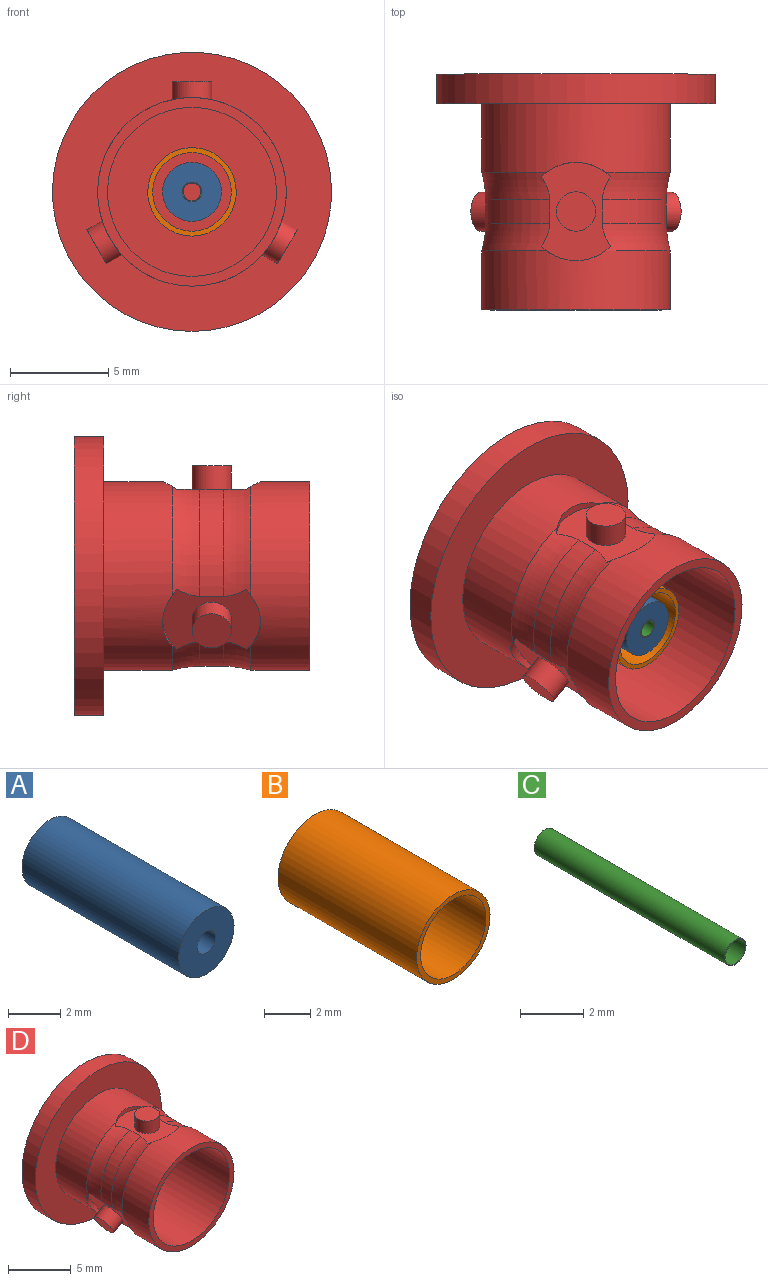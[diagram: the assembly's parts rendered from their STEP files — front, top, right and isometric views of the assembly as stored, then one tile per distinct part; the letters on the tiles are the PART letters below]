
ASSEMBLY  parts=4 mates=3
PART A: 4 faces, bbox 3x8.5x3 mm
  f0: cylinder r=0.5mm len=8.5mm, axis (0,1,0), area 26.7mm2, adj f2,f3
  f1: cylinder r=1.5mm len=8.5mm, axis (0,1,0), area 80.1mm2, adj f2,f3
  f2: plane 3x3mm, normal (0,-1,0), area 6.3mm2, adj f0,f1
  f3: plane 3x3mm, normal (0,1,0), area 6.3mm2, adj f0,f1
PART B: 4 faces, bbox 4.5x8.5x4.5 mm
  f0: cylinder r=2mm len=8.5mm, axis (0,1,0), area 106.8mm2, adj f2,f3
  f1: cylinder r=2.25mm len=8.5mm, axis (0,1,0), area 120.2mm2, adj f2,f3
  f2: plane 4.5x4.5mm, normal (0,-1,0), area 3.3mm2, adj f0,f1
  f3: plane 4.5x4.5mm, normal (0,1,0), area 3.3mm2, adj f0,f1
PART C: 4 faces, bbox 1x8.5x1 mm
  f0: cylinder r=0.45mm len=8.5mm, axis (0,1,0), area 24mm2, adj f2,f3
  f1: cylinder r=0.47mm len=8.5mm, axis (0,1,0), area 25.4mm2, adj f2,f3
  f2: plane 0.95x0.95mm, normal (0,-1,0), area 0.1mm2, adj f0,f1
  f3: plane 0.95x0.95mm, normal (0,1,0), area 0.1mm2, adj f0,f1
PART D: 32 faces, bbox 14.2x12x14.2 mm
  f0: plane 2x1.73mm, normal (0.87,0,-0.5), area 3.1mm2, adj f1
  f1: cylinder r=1mm len=2.33mm, axis (0.87,0,-0.5), area 7.5mm2, adj f0,f8
  f2: plane 2x1.73mm, normal (-0.87,0,-0.5), area 3.1mm2, adj f3
  f3: cylinder r=1mm len=2.33mm, axis (-0.87,0,-0.5), area 7.5mm2, adj f2,f6
  f4: cylinder r=4.8mm len=9.6mm, axis (0,1,0), area 102.5mm2, adj f5,f7,f9,f17,f27,f28,f30
  f5: cylinder r=2.5mm len=3.25mm, axis (-0.87,0,-0.5), area 1.1mm2, adj f4,f6,f27,f28
  f6: plane 5x3.05mm, normal (-0.87,0,-0.5), area 10.6mm2, adj f3,f5,f19,f23,f24,f25,f26,f27
  f7: cylinder r=2.5mm len=3.25mm, axis (0.87,0,-0.5), area 1.1mm2, adj f4,f8,f27,f30
  f8: plane 5x3.05mm, normal (0.87,0,-0.5), area 10.6mm2, adj f1,f7,f20,f22,f24,f25,f27,f29
  f9: cylinder r=2.5mm len=3.52mm, axis (0,0,1), area 1.1mm2, adj f4,f10,f28,f30
  f10: plane 5x3.52mm, normal (0,0,1), area 10.6mm2, adj f9,f11,f21,f22,f23,f26,f28,f29
  f11: cylinder r=1mm len=2mm, axis (0,0,1), area 7.5mm2, adj f10,f31
  f12: cylinder r=4.8mm len=9.6mm, axis (0,1,0), area 87.4mm2, adj f14,f19,f20,f21,f25,f26,f29
  f13: cylinder r=4.3mm len=10.5mm, axis (0,1,0), area 283.7mm2, adj f14,f18
  f14: plane 9.6x9.6mm, normal (0,-1,0), area 14.3mm2, adj f12,f13
  f15: plane 14.2x14.2mm, normal (0,1,0), area 158.4mm2, adj f16
  f16: cylinder r=7.1mm len=14.2mm, axis (0,1,0), area 66.9mm2, adj f15,f17
  f17: plane 14.2x14.2mm, normal (0,-1,0), area 86mm2, adj f4,f16
  f18: plane 8.6x8.6mm, normal (0,-1,0), area 58.1mm2, adj f13
  f19: cylinder r=2.5mm len=3.25mm, axis (-0.87,0,-0.5), area 1.1mm2, adj f6,f12,f25,f26
  f20: cylinder r=2.5mm len=3.25mm, axis (0.87,0,-0.5), area 1.1mm2, adj f8,f12,f25,f29
  f21: cylinder r=2.5mm len=3.52mm, axis (0,0,1), area 1.1mm2, adj f10,f12,f26,f29
  f22: cylinder r=4.6mm len=5.44mm, axis (0,-1,0), area 8.3mm2, adj f8,f10,f29,f30
  f23: cylinder r=4.6mm len=5.44mm, axis (0,-1,0), area 8.3mm2, adj f6,f10,f26,f28
  f24: cylinder r=4.6mm len=6.28mm, axis (0,-1,0), area 8.3mm2, adj f6,f8,f25,f27
  f25: torus R=9.6mm, axis (0,-1,0), area 9.5mm2, adj f6,f8,f12,f19,f20,f24
  f26: torus R=9.6mm, axis (0,-1,0), area 9.5mm2, adj f6,f10,f12,f19,f21,f23
  f27: torus R=9.6mm, axis (0,1,0), area 9.5mm2, adj f4,f5,f6,f7,f8,f24
  f28: torus R=9.6mm, axis (0,1,0), area 9.5mm2, adj f4,f5,f6,f9,f10,f23
  f29: torus R=9.6mm, axis (0,-1,0), area 9.5mm2, adj f8,f10,f12,f20,f21,f22
  f30: torus R=9.6mm, axis (0,1,0), area 9.5mm2, adj f4,f7,f8,f9,f10,f22
  f31: plane 2x2mm, normal (0,0,1), area 3.1mm2, adj f11
PLACE A t=(4.85,6.05,-11.19)mm
PLACE B t=(4.85,6.05,-11.19)mm
PLACE C t=(4.85,6.05,-11.19)mm
PLACE D t=(4.85,6.05,-11.19)mm
MATE fastened D.f4 <-> A.f0  axis (0,-1,0) through (9.2,4.55,-7.52)mm
MATE fastened D.f4 <-> B.f0  axis (0,-1,0) through (9.2,4.55,-7.52)mm
MATE fastened D.f4 <-> C.f0  axis (0,-1,0) through (9.2,4.55,-7.52)mm
